# Revit family: INGROUND 18W SIMETRICA_EM18SW.1.20
name_source: partatom
category: Luminarias
units: mm (PartAtom-declared; Revit-internal decimal feet)

## family parameters
Compartido = No
Corte con vacíos al cargar = No
Cota de conector redondo = Diámetro de uso
Origen de luz = Sí
Punto de cálculo de habitación = No
Se basa en plano de trabajo = Sí
Siempre vertical = No
Tipo de pieza = Normal

## types (1)
- EMP_EM18SW.1.20
    Cambio de temperatura de color de luz atenuada = <Ninguno>
    Comentarios de vataje = 100-277V
    Descripción = LUMINARIA TIPO CIRCULAR PARA EMPOTRAR EN PISO CON CUERPO DE ALUMINIO FUNDIDO A PRESION CUBIERTO CON POLVO GRIS OSCURO, CON CUBIERTA DE ACERO INOXIDABLE Y VIDRIO TEMPLADO DE 8MM, HOUSING TIPO ABS DE 171.5MM DE DIAMETRO Y 123.6MM DE PROFUNDO. CUENTA CON 6 LED TIPO NICHIA CON UNA POTENCIA TOTAL DE 18.6W, A UNA TEMPERATURA EN BLANCO CALIDO 3000K CON 1605 LUMENES, 156mA EN CORRIENTE DE OPERACIÓN, IP67, IK09, IRC 80, DISPONIBLE PARA ATENUAR EN TRIAC (OPCIONAL), APERTURA EN 20 GRADOS POR PROYECTO, ALIMENTADA A 100-277V
    Elevación por defecto = 0 mm  [stored 0 ft]
    Fabricante = BRILLANT
    Filtro de color = 16777215
    Longitud de símbolo de origen de luz = 500 mm  [stored 1.64042 ft]
    Lámpara = NICHIA
    Modelo = EM18SW.1.20
    Watt per fixture = 18.6
    Ángulo de campo de foco = 20.00°
    Ángulo de enfoque = 20.00°
    Ángulo de inclinación = 105.00°

note: [stored X ft] marks values corroborated as IEEE doubles in the binary element streams (Revit-internal decimal feet)

## geometry (parser evidence)
native form markers: Blend x2
no freeform markers — native parametric forms only
